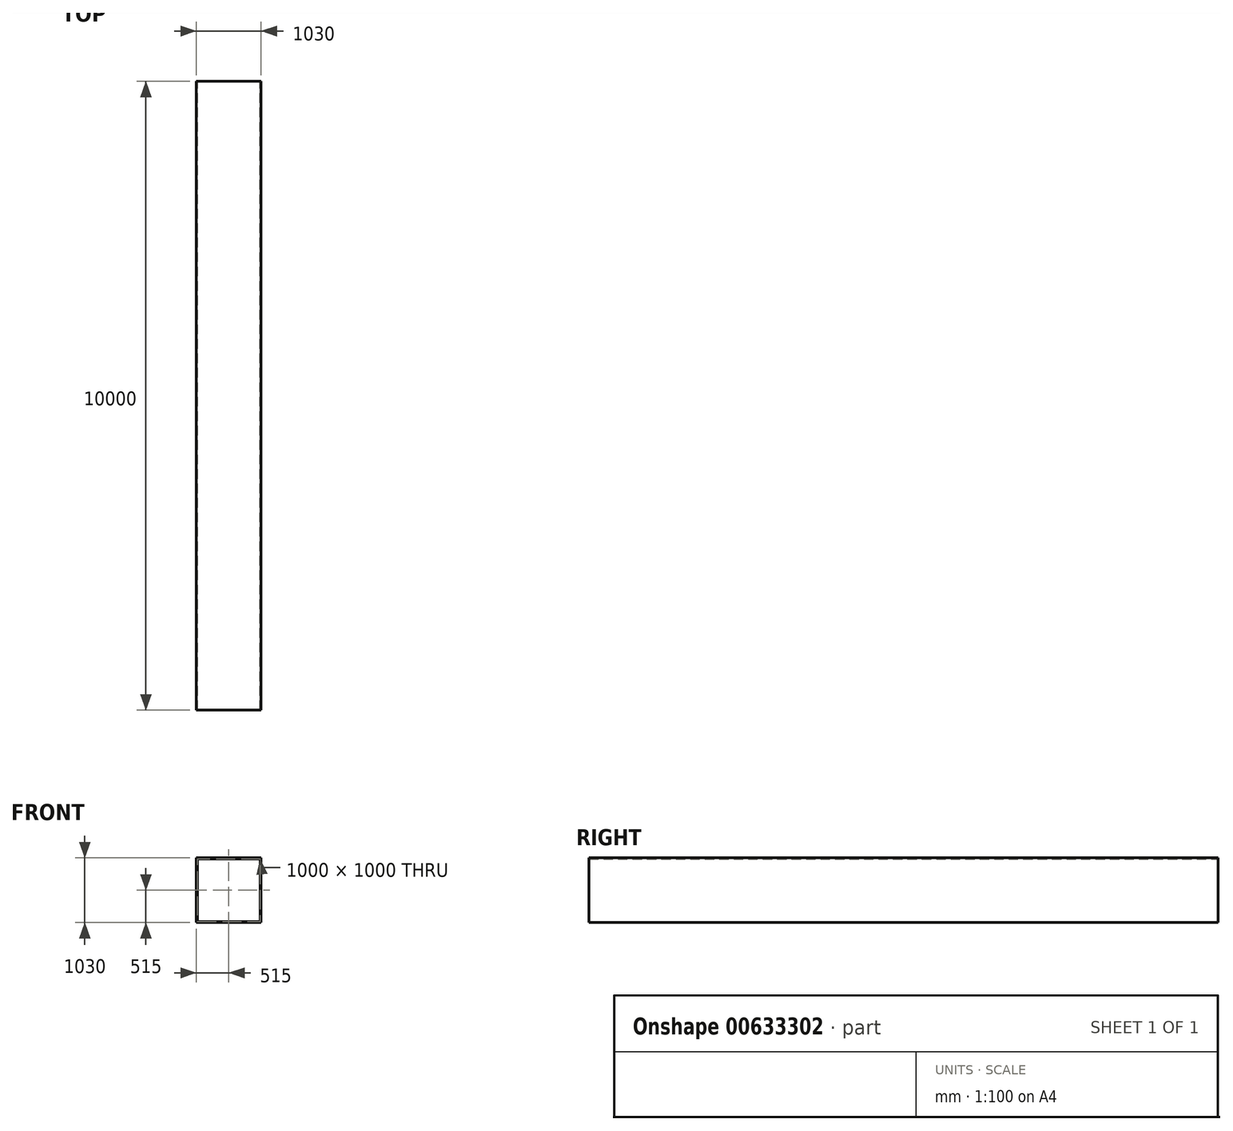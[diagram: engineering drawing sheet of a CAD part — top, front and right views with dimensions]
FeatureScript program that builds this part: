
annotation { "Feature Type Name" : "Feature", "Feature Type Description" : "" }
export const myFeature = defineFeature(function(context is Context, id is Id, definition is map)
    precondition{}
    {
        {
            var Q0;
            Q0=qCreatedBy(makeId("Front.planeOp"),FACE);
            var sketch = newSketch(context, id + "F0", { "sketchPlane" : qUnion([Q0])});
            skLineSegment(sketch, "E0.bottom", {"start": v(500, -500) * mm, "end": v(-500, -500) * mm});
            skLineSegment(sketch, "E0.top", {"start": v(500, 500) * mm, "end": v(-500, 500) * mm});
            skLineSegment(sketch, "E0.left", {"start": v(500, -500) * mm, "end": v(500, 500) * mm});
            skLineSegment(sketch, "E0.right", {"start": v(-500, -500) * mm, "end": v(-500, 500) * mm});
            skPoint(sketch, "E0.middle", {"position": v(0, 0) * mm});
            skLineSegment(sketch, "E1.bottom", {"start": v(515, 515) * mm, "end": v(-515, 515) * mm});
            skLineSegment(sketch, "E1.top", {"start": v(515, -515) * mm, "end": v(-515, -515) * mm});
            skLineSegment(sketch, "E1.left", {"start": v(515, 515) * mm, "end": v(515, -515) * mm});
            skLineSegment(sketch, "E1.right", {"start": v(-515, 515) * mm, "end": v(-515, -515) * mm});
            skSolve(sketch);
        }
        {
            var Q0;
            Q0 = qSketchRegion(id + "F0", true);
            extrude(context, id + "F1", {"entities" : qUnion([Q0]), "endBound" : BoundingType.SYMMETRIC, "depth" : 10000 * mm, "offsetDistance" : 25 * mm});
        }
    });
